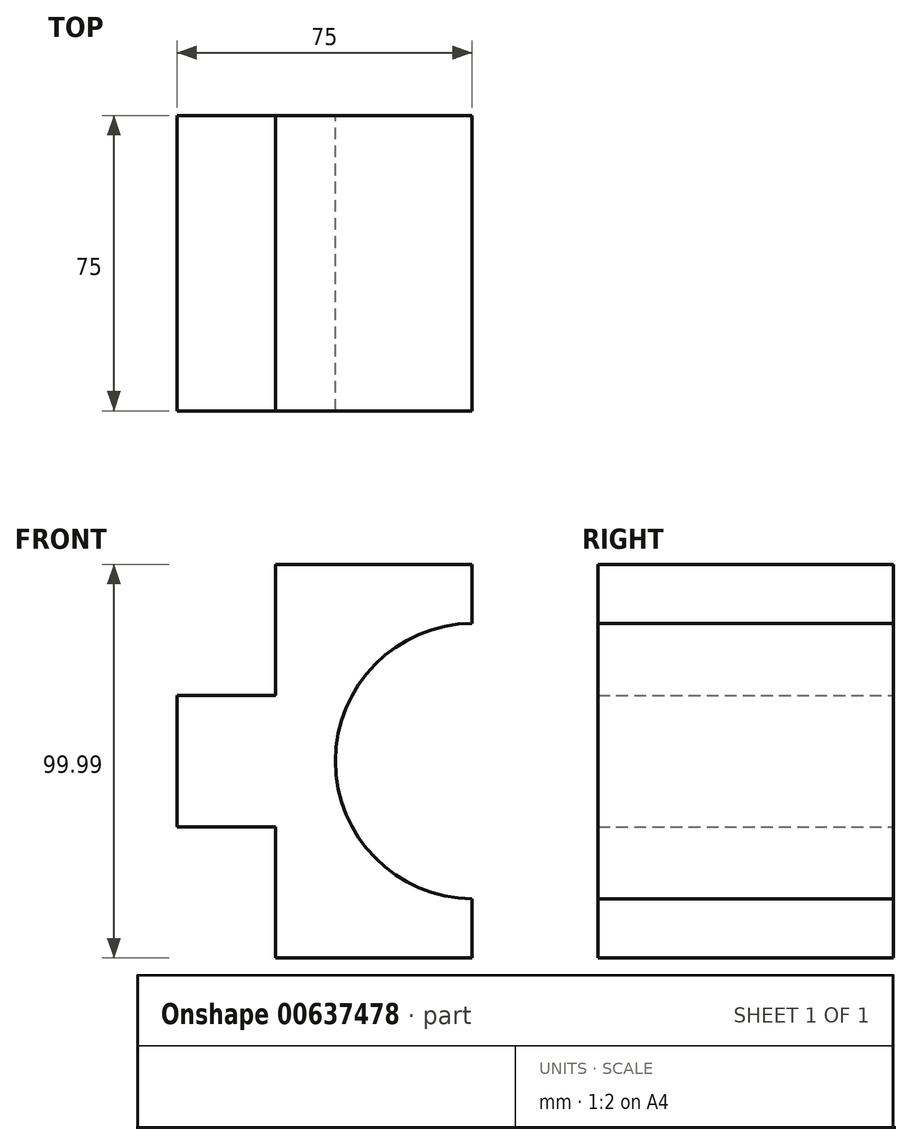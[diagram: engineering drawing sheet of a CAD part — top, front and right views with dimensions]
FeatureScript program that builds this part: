
annotation { "Feature Type Name" : "Feature", "Feature Type Description" : "" }
export const myFeature = defineFeature(function(context is Context, id is Id, definition is map)
    precondition{}
    {
        {
            var Q0;
            Q0=qCreatedBy(makeId("Front.planeOp"),FACE);
            var sketch = newSketch(context, id + "F0", { "sketchPlane" : qUnion([Q0])});
            skLineSegment(sketch, "E0", {"start": v(0, 0) * mm, "end": v(0, -15) * mm});
            skLineSegment(sketch, "E1", {"start": v(0, -15) * mm, "end": v(-50, -15) * mm});
            skLineSegment(sketch, "E2", {"start": v(-50, -15) * mm, "end": v(-50, 18.33) * mm});
            skLineSegment(sketch, "E3", {"start": v(-50, 18.33) * mm, "end": v(-75, 18.33) * mm});
            skLineSegment(sketch, "E4", {"start": v(-75, 18.33) * mm, "end": v(-75, 51.66) * mm});
            skLineSegment(sketch, "E5", {"start": v(-75, 51.66) * mm, "end": v(-50, 51.66) * mm});
            skLineSegment(sketch, "E6", {"start": v(-50, 51.66) * mm, "end": v(-50, 84.99) * mm});
            skLineSegment(sketch, "E7", {"start": v(-50, 84.99) * mm, "end": v(0, 84.99) * mm});
            skLineSegment(sketch, "E8", {"start": v(0, 84.99) * mm, "end": v(0, 69.99) * mm});
            skArc(sketch, "E9", {"start": v(0, 69.99) * mm, "mid": v(-34.74, 35) * mm, "end": v(0, 0) * mm});
            skSolve(sketch);
        }
        {
            var Q0;
            Q0 = qSketchRegion(id + "F0", true);
            extrude(context, id + "F1", {"entities" : qUnion([Q0]), "depth" : 75 * mm, "offsetDistance" : 25 * mm});
        }
    });
